# Revit family: Shower-Valve_Trim-KALLISTA-Per_Se-P24732T_1
name_source: partatom
category: Specialty Equipment
units: mm (PartAtom-declared; Revit-internal decimal feet)

## family parameters
Cut with Voids When Loaded = No
Host = Face
OmniClass Number = 23.31.25.00
OmniClass Title = Toilet and Bath Specialties
Part Type = Normal
Room Calculation Point = No
Round Connector Dimension = Use Diameter
Shared = No

## types (5) — shared parameters
ADA Compliant = No
Assembly Code = C1030200
Date Modified = 03/28/2023
Default Elevation = 42"
Description = THERMOSTATIC TRIM
Handle Clearance 1 = 1 9/16"
Handle Clearance 2 = 2 3/4"
Height = 7 1/16"
Length = 4 3/16"
Manufacturer = Kallista Co.
Master Format 2014 = 10 28 00
Master Format 2014 Name = Toilet, Bath, and Laundry Accessories
Material = Premium Metal Construction
Product Documentation Link = https://resources.kohler.com
Product Name = Per Se
URL = https://www.kallista.com
WaterSense Certified = No
Width = 5 1/2"

## per-type parameters (varying)
| type | Finish | Model | Product Page URL | Type |
| AF-French Gold | Kallista-Metal-AF-French_Gold | P24732T-LV-AF |  | 1 |
| BAF-Brushed French Gold | Kallista-Metal-BAF-Brushed_French_Gold | P24732T-LV-BAF |  | 2 |
| BN-Brushed Nickel | Kallista-Metal-BN-Brushed_Nickel | P24732T-LV-BN |  | 3 |
| CP-Chrome | Kallista-Metal-CP-Chrome | P24732T-LV-CP | https://www.kallista.com | 4 |
| SN-Polished Nickel | Kallista-Metal-SN-Polished_Nickel | P24732T-LV-SN |  | 5 |

## geometry (parser evidence)
native form markers: Sweep x4
no freeform markers — native parametric forms only
